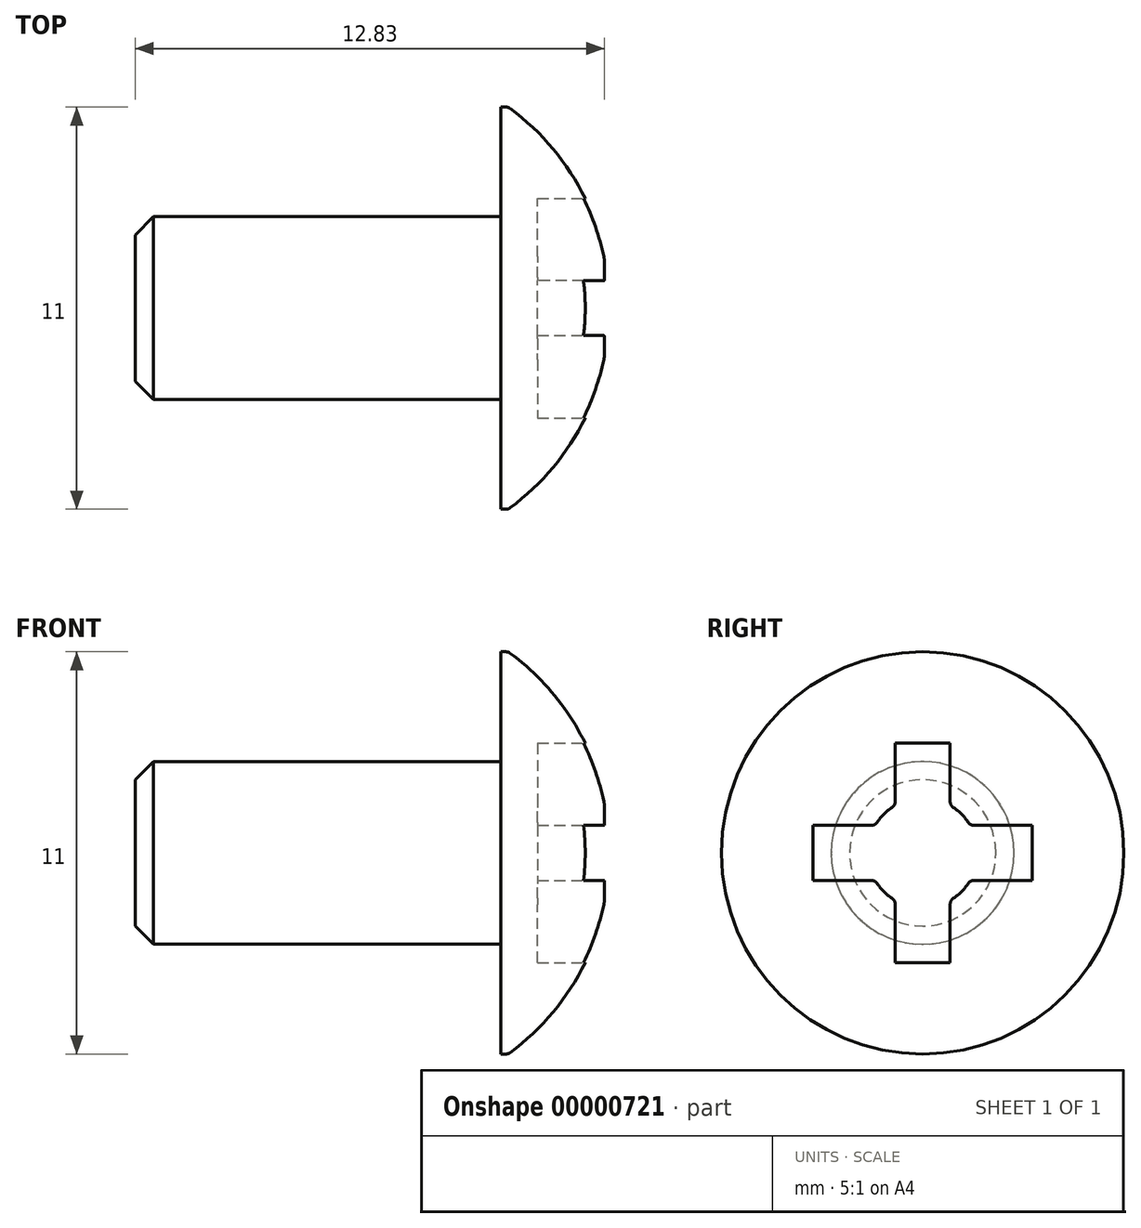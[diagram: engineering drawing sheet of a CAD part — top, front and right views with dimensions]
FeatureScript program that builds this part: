
annotation { "Feature Type Name" : "Feature", "Feature Type Description" : "" }
export const myFeature = defineFeature(function(context is Context, id is Id, definition is map)
    precondition{}
    {
        {
            var Q0;
            Q0=qCreatedBy(makeId("Front.planeOp"),FACE);
            var sketch = newSketch(context, id + "F0", { "sketchPlane" : qUnion([Q0])});
            skLineSegment(sketch, "E0", {"start": v(0, 2.5) * mm, "end": v(0, 5.5) * mm});
            skLineSegment(sketch, "E1", {"start": v(0, 2.5) * mm, "end": v(-10, 2.5) * mm});
            skLineSegment(sketch, "E2", {"start": v(-10, 2.5) * mm, "end": v(-10, 0) * mm});
            skLineSegment(sketch, "E3", {"start": v(-10, 0) * mm, "end": v(3, 0) * mm});
            skLineSegment(sketch, "E4", {"start": v(0, 0) * mm, "end": v(32.43, 0) * mm, "construction": true});
            skLineSegment(sketch, "E5", {"start": v(0, 5.5) * mm, "end": v(0.2, 5.5) * mm});
            skArc(sketch, "E6", {"start": v(3, 0) * mm, "mid": v(2.26, 3.09) * mm, "end": v(0.2, 5.5) * mm});
            skLineSegment(sketch, "E7", {"start": v(3, 0) * mm, "end": v(3, 6.78) * mm, "construction": true});
            skSolve(sketch);
        }
        {
            var Q0;
            Q0=makeQuery(id+"F0.imprint","IMPRINT",FACE,{"disambiguationData":[TD([[makeQuery(id+"F0.imprint","IMPRINT",EDGE,{"derivedFrom":sQuery(id+"F0.wireOp",EDGE,"E0")}),-1.0]])]});
            var Q1;
            Q1=sQuery(id+"F0.wireOp",EDGE,"E4");
            revolve(context, id + "F1", {"entities" : qUnion([Q0]), "axis" : qUnion([Q1]), "revolveType" : RevolveType.FULL});
        }
        {
            var Q0;
            Q0=makeQuery(id+"F1.opRevolve","SWEPT_EDGE",EDGE,{"disambiguationData":[OSD([sQuery(id+"F0.wireOp",EDGE,"E1"),sQuery(id+"F0.wireOp",EDGE,"E2")])]});
            chamfer(context, id + "F2", {"entities" : qUnion([Q0]), "width" : .5 * mm, "tangentPropagation" : true});
        }
        {
            var Q0;
            Q0=qCreatedBy(makeId("Right.planeOp"),FACE);
            cPlane(context, id + "F3", {"entities" : qUnion([Q0]), "cplaneType" : CPlaneType.OFFSET, "offset" : 3 * mm, "width" : 150 * mm, "height" : 150 * mm});
        }
        {
            var Q0;
            Q0=qCreatedBy(id+"F3.planeOp",FACE);
            var sketch = newSketch(context, id + "F4", { "sketchPlane" : qUnion([Q0])});
            skLineSegment(sketch, "E8.bottom", {"start": v(0, 0) * mm, "end": v(3, 0) * mm, "construction": true});
            skLineSegment(sketch, "E8.top", {"start": v(0, 3) * mm, "end": v(0.75, 3) * mm});
            skLineSegment(sketch, "E8.left", {"start": v(0, 0) * mm, "end": v(0, 3) * mm, "construction": true});
            skLineSegment(sketch, "E8.right", {"start": v(3, 0) * mm, "end": v(3, 0.75) * mm});
            skLineSegment(sketch, "E9", {"start": v(0.75, 3) * mm, "end": v(0.75, 1.3) * mm});
            skLineSegment(sketch, "E10", {"start": v(1.3, 0.75) * mm, "end": v(3, 0.75) * mm});
            skArc(sketch, "E11", {"start": v(1.3, 0.75) * mm, "mid": v(1.06, 1.06) * mm, "end": v(0.75, 1.3) * mm});
            skLineSegment(sketch, "E12.0.MirrorCS", {"start": v(0, -3) * mm, "end": v(0.75, -3) * mm});
            skLineSegment(sketch, "E13.0.MirrorCS", {"start": v(0.75, -3) * mm, "end": v(0.75, -1.3) * mm});
            skArc(sketch, "E14.0.MirrorCS", {"start": v(1.3, -0.75) * mm, "mid": v(1.06, -1.06) * mm, "end": v(0.75, -1.3) * mm});
            skLineSegment(sketch, "E15.0.MirrorCS", {"start": v(1.3, -0.75) * mm, "end": v(3, -0.75) * mm});
            skLineSegment(sketch, "E16.0.MirrorCS", {"start": v(3, 0) * mm, "end": v(3, -0.75) * mm});
            skLineSegment(sketch, "E17.0.MirrorCS", {"start": v(0, 3) * mm, "end": v(-0.75, 3) * mm});
            skLineSegment(sketch, "E18.0.MirrorCS", {"start": v(-0.75, 3) * mm, "end": v(-0.75, 1.3) * mm});
            skArc(sketch, "E19.0.MirrorCS", {"start": v(-1.3, 0.75) * mm, "mid": v(-1.06, 1.06) * mm, "end": v(-0.75, 1.3) * mm});
            skLineSegment(sketch, "E20.0.MirrorCS", {"start": v(-1.3, 0.75) * mm, "end": v(-3, 0.75) * mm});
            skLineSegment(sketch, "E21.0.MirrorCS", {"start": v(-3, 0) * mm, "end": v(-3, 0.75) * mm});
            skLineSegment(sketch, "E22.0.MirrorCS", {"start": v(-3, 0) * mm, "end": v(-3, -0.75) * mm});
            skLineSegment(sketch, "E23.0.MirrorCS", {"start": v(-1.3, -0.75) * mm, "end": v(-3, -0.75) * mm});
            skArc(sketch, "E24.0.MirrorCS", {"start": v(-1.3, -0.75) * mm, "mid": v(-1.06, -1.06) * mm, "end": v(-0.75, -1.3) * mm});
            skLineSegment(sketch, "E25.0.MirrorCS", {"start": v(-0.75, -3) * mm, "end": v(-0.75, -1.3) * mm});
            skLineSegment(sketch, "E26.0.MirrorCS", {"start": v(0, -3) * mm, "end": v(-0.75, -3) * mm});
            skSolve(sketch);
        }
        {
            var Q0;
            Q0=makeQuery(id+"F4.imprint","IMPRINT",FACE,{"disambiguationData":[TD([[makeQuery(id+"F4.imprint","IMPRINT",EDGE,{"derivedFrom":sQuery(id+"F4.wireOp",EDGE,"E8.top")}),-1.0]])]});
            extrude(context, id + "F5", {"entities" : qUnion([Q0]), "operationType" : NewBodyOperationType.REMOVE, "oppositeDirection" : true, "depth" : 2 * mm});
        }
        {
            var Q0;
            Q0=makeQuery(id+"F5.boolean.opBoolean","COPY",EDGE,{"derivedFrom":makeQuery(id+"F5.opExtrude","SWEPT_EDGE",EDGE,{"disambiguationData":[OSD([sQuery(id+"F4.wireOp",EDGE,"E9"),sQuery(id+"F4.wireOp",EDGE,"E11")])]})});
            var Q1;
            Q1=makeQuery(id+"F5.boolean.opBoolean","COPY",EDGE,{"derivedFrom":makeQuery(id+"F5.opExtrude","SWEPT_EDGE",EDGE,{"disambiguationData":[OSD([sQuery(id+"F4.wireOp",EDGE,"E10"),sQuery(id+"F4.wireOp",EDGE,"E11")])]})});
            var Q2;
            Q2=makeQuery(id+"F5.boolean.opBoolean","COPY",EDGE,{"derivedFrom":makeQuery(id+"F5.opExtrude","SWEPT_EDGE",EDGE,{"disambiguationData":[OSD([sQuery(id+"F4.wireOp",EDGE,"E14.0.MirrorCS"),sQuery(id+"F4.wireOp",EDGE,"E15.0.MirrorCS")])]})});
            var Q3;
            Q3=makeQuery(id+"F5.boolean.opBoolean","COPY",EDGE,{"derivedFrom":makeQuery(id+"F5.opExtrude","SWEPT_EDGE",EDGE,{"disambiguationData":[OSD([sQuery(id+"F4.wireOp",EDGE,"E13.0.MirrorCS"),sQuery(id+"F4.wireOp",EDGE,"E14.0.MirrorCS")])]})});
            var Q4;
            Q4=makeQuery(id+"F5.boolean.opBoolean","COPY",EDGE,{"derivedFrom":makeQuery(id+"F5.opExtrude","SWEPT_EDGE",EDGE,{"disambiguationData":[OSD([sQuery(id+"F4.wireOp",EDGE,"E19.0.MirrorCS"),sQuery(id+"F4.wireOp",EDGE,"E20.0.MirrorCS")])]})});
            var Q5;
            Q5=makeQuery(id+"F5.boolean.opBoolean","COPY",EDGE,{"derivedFrom":makeQuery(id+"F5.opExtrude","SWEPT_EDGE",EDGE,{"disambiguationData":[OSD([sQuery(id+"F4.wireOp",EDGE,"E18.0.MirrorCS"),sQuery(id+"F4.wireOp",EDGE,"E19.0.MirrorCS")])]})});
            var Q6;
            Q6=makeQuery(id+"F5.boolean.opBoolean","COPY",EDGE,{"derivedFrom":makeQuery(id+"F5.opExtrude","SWEPT_EDGE",EDGE,{"disambiguationData":[OSD([sQuery(id+"F4.wireOp",EDGE,"E24.0.MirrorCS"),sQuery(id+"F4.wireOp",EDGE,"E25.0.MirrorCS")])]})});
            var Q7;
            Q7=makeQuery(id+"F5.boolean.opBoolean","COPY",EDGE,{"derivedFrom":makeQuery(id+"F5.opExtrude","SWEPT_EDGE",EDGE,{"disambiguationData":[OSD([sQuery(id+"F4.wireOp",EDGE,"E23.0.MirrorCS"),sQuery(id+"F4.wireOp",EDGE,"E24.0.MirrorCS")])]})});
            fillet(context, id + "F6", {"entities" : qUnion([Q0, Q1, Q2, Q3, Q4, Q5, Q6, Q7]), "radius" : .2 * mm, "tangentPropagation" : true, "allowEdgeOverflow" : false});
        }
        {
            var Q0;
            Q0=makeQuery(id+"F1.opRevolve","SWEPT_EDGE",EDGE,{"disambiguationData":[OSD([sQuery(id+"F0.wireOp",EDGE,"E5"),sQuery(id+"F0.wireOp",EDGE,"E6")])]});
            fillet(context, id + "F7", {"entities" : qUnion([Q0]), "radius" : .2 * mm, "tangentPropagation" : true, "allowEdgeOverflow" : false});
        }
    });
